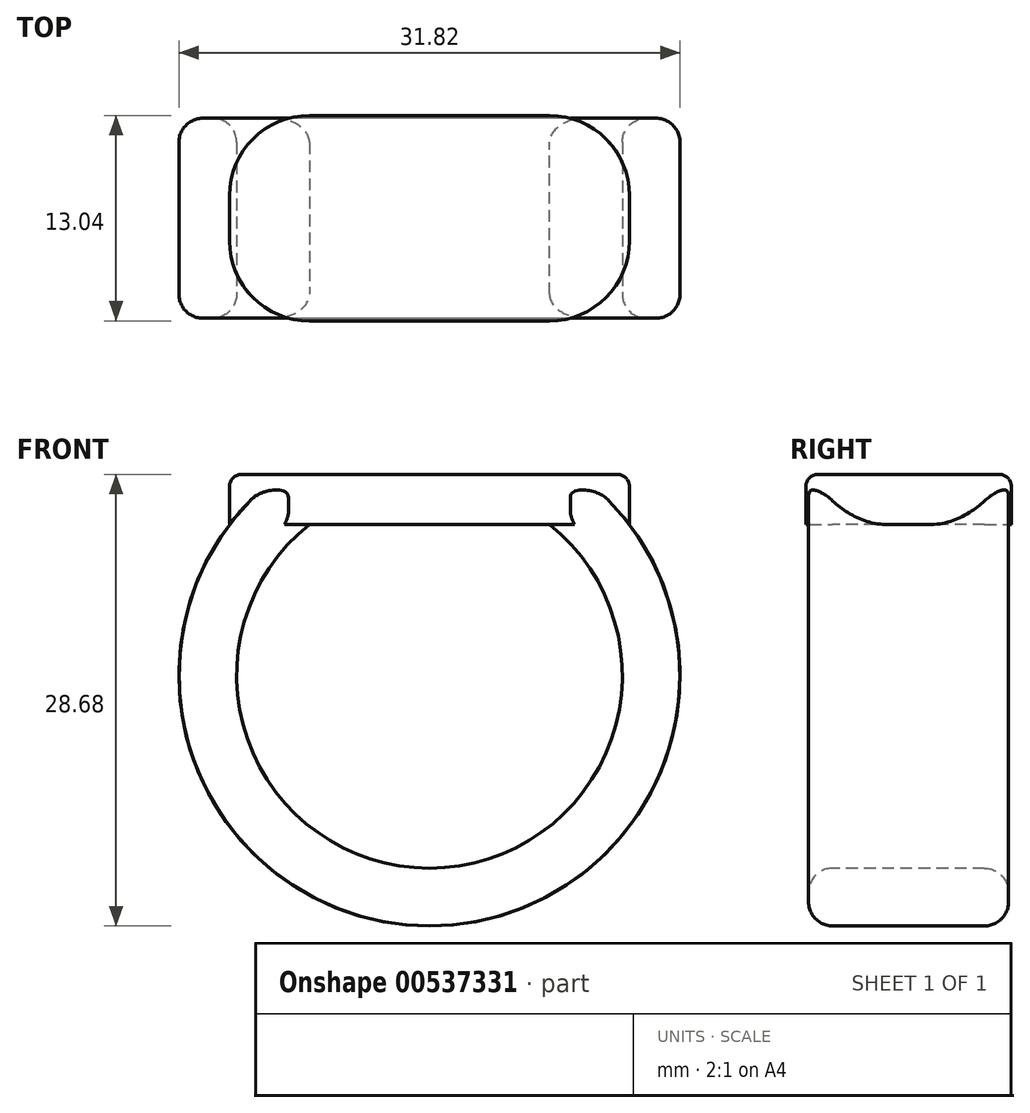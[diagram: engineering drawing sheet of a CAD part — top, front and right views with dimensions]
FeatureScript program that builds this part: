
annotation { "Feature Type Name" : "Feature", "Feature Type Description" : "" }
export const myFeature = defineFeature(function(context is Context, id is Id, definition is map)
    precondition{}
    {
        {
            var Q0;
            Q0=qCreatedBy(makeId("Top.planeOp"),FACE);
            var sketch = newSketch(context, id + "F0", { "sketchPlane" : qUnion([Q0])});
            skLineSegment(sketch, "E0.bottom", {"start": v(12.7, 6.52) * mm, "end": v(-12.7, 6.52) * mm});
            skLineSegment(sketch, "E0.top", {"start": v(12.7, -6.52) * mm, "end": v(-12.7, -6.52) * mm});
            skLineSegment(sketch, "E0.left", {"start": v(12.7, 6.52) * mm, "end": v(12.7, -6.52) * mm});
            skLineSegment(sketch, "E0.right", {"start": v(-12.7, 6.52) * mm, "end": v(-12.7, -6.52) * mm});
            skPoint(sketch, "E0.middle", {"position": v(0, 0) * mm});
            skSolve(sketch);
        }
        {
            var Q0;
            Q0 = qSketchRegion(id + "F0", true);
            extrude(context, id + "F1", {"entities" : qUnion([Q0]), "depth" : 3.17 * mm, "offsetDistance" : 25.4 * mm});
        }
        {
            var Q0;
            Q0=qCreatedBy(makeId("Front.planeOp"),FACE);
            var sketch = newSketch(context, id + "F2", { "sketchPlane" : qUnion([Q0])});
            skArc(sketch, "E1", {"start": v(-10.16, 0) * mm, "mid": v(0, -23.56) * mm, "end": v(10.16, 0) * mm});
            skSolve(sketch);
        }
        {
            var Q0;
            Q0=makeQuery(id+"F1.opExtrude","CAP_FACE",FACE,{"disambiguationData":[OSD([sQuery(id+"F0.wireOp",EDGE,"E0.bottom"),sQuery(id+"F0.wireOp",EDGE,"E0.top"),sQuery(id+"F0.wireOp",EDGE,"E0.left"),sQuery(id+"F0.wireOp",EDGE,"E0.right")])],"isStart":true});
            var sketch = newSketch(context, id + "F3", { "sketchPlane" : qUnion([Q0])});
            skLineSegment(sketch, "E2.bottom", {"start": v(-12.7, -6.35) * mm, "end": v(-7.62, -6.35) * mm});
            skLineSegment(sketch, "E2.top", {"start": v(-12.7, 6.35) * mm, "end": v(-7.62, 6.35) * mm});
            skLineSegment(sketch, "E2.left", {"start": v(-12.7, -6.35) * mm, "end": v(-12.7, 6.35) * mm});
            skLineSegment(sketch, "E2.right", {"start": v(-7.62, -6.35) * mm, "end": v(-7.62, 6.35) * mm});
            skPoint(sketch, "E2.middle", {"position": v(-10.16, 0) * mm});
            skSolve(sketch);
        }
        {
            var Q0;
            Q0 = qSketchRegion(id + "F3", true);
            var Q1;
            Q1 = qConstructionFilter(qBodyType(qCreatedBy(id + "F2" ,EDGE), BodyType.WIRE), ConstructionObject.NO);
            sweep(context, id + "F4", {"operationType" : NewBodyOperationType.ADD, "profiles" : qUnion([Q0]), "path" : qUnion([Q1])});
        }
        {
            var Q0;
            Q0=qCreatedBy(makeId("Front.planeOp"),FACE);
            var sketch = newSketch(context, id + "F5", { "sketchPlane" : qUnion([Q0])});
            skLineSegment(sketch, "E3.0", {"start": v(10.16, 0) * mm, "end": v(7.62, 0) * mm});
            skArc(sketch, "E3.1", {"start": v(10.01, -2.54) * mm, "mid": v(8.9, -1.18) * mm, "end": v(7.62, 0) * mm});
            skLineSegment(sketch, "E3.2", {"start": v(10.01, -2.54) * mm, "end": v(10.16, 0) * mm});
            skPoint(sketch, "E4.orphan", {"position": v(-7.62, 0) * mm});
            skPoint(sketch, "E5.orphan", {"position": v(12.7, 0) * mm});
            skPoint(sketch, "E6.trimOffspring.end.orphan", {"position": v(-12.7, 0) * mm});
            skSolve(sketch);
        }
        {
            var Q0;
            Q0 = qSketchRegion(id + "F5", true);
            var Q1;
            Q1=makeQuery(id+"F4.opSweep","SWEPT_FACE",FACE,{"disambiguationData":[OSD([sQuery(id+"F2.wireOp",EDGE,"E1"),sQuery(id+"F3.wireOp",EDGE,"E2.top")])]});
            var Q2;
            Q2=makeQuery(id+"F4.opSweep","SWEPT_FACE",FACE,{"disambiguationData":[OSD([sQuery(id+"F2.wireOp",EDGE,"E1"),sQuery(id+"F3.wireOp",EDGE,"E2.bottom")])]});
            extrude(context, id + "F6", {"entities" : qUnion([Q0]), "operationType" : NewBodyOperationType.ADD, "endBound" : BoundingType.UP_TO_SURFACE, "depth" : 25.4 * mm, "endBoundEntityFace" : qUnion([Q1]), "offsetDistance" : 25.4 * mm, "hasSecondDirection" : true, "secondDirectionBound" : SecondDirectionBoundingType.UP_TO_SURFACE, "secondDirectionOppositeDirection" : true, "secondDirectionDepth" : 25.4 * mm, "secondDirectionBoundEntityFace" : qUnion([Q2])});
        }
        {
            var Q0;
            Q0=makeQuery(id+"F1.opExtrude","SWEPT_EDGE",EDGE,{"disambiguationData":[OSD([sQuery(id+"F0.wireOp",EDGE,"E0.top"),sQuery(id+"F0.wireOp",EDGE,"E0.left")])]});
            var Q1;
            Q1=makeQuery(id+"F1.opExtrude","SWEPT_EDGE",EDGE,{"disambiguationData":[OSD([sQuery(id+"F0.wireOp",EDGE,"E0.bottom"),sQuery(id+"F0.wireOp",EDGE,"E0.left")])]});
            var Q2;
            Q2=makeQuery(id+"F1.opExtrude","SWEPT_EDGE",EDGE,{"disambiguationData":[OSD([sQuery(id+"F0.wireOp",EDGE,"E0.bottom"),sQuery(id+"F0.wireOp",EDGE,"E0.right")])]});
            var Q3;
            Q3=makeQuery(id+"F1.opExtrude","SWEPT_EDGE",EDGE,{"disambiguationData":[OSD([sQuery(id+"F0.wireOp",EDGE,"E0.top"),sQuery(id+"F0.wireOp",EDGE,"E0.right")])]});
            fillet(context, id + "F7", {"entities" : qUnion([Q0, Q1, Q2, Q3]), "radius" : 5.08 * mm, "tangentPropagation" : true, "allowEdgeOverflow" : false});
        }
        {
            var Q0;
            {var subQ0=sQuery(id+"F3.wireOp",EDGE,"E2.top");var subQ1=sQuery(id+"F2.wireOp",EDGE,"E1");Q0=makeQuery(id+"F6.boolean.opBoolean","MERGE",EDGE,{"derivedFrom":[makeQuery(id+"F4.opSweep","SWEPT_EDGE",EDGE,{"disambiguationData":[OSD([subQ1,subQ0,sQuery(id+"F3.wireOp",EDGE,"E2.right")])]}),makeQuery(id+"F6.opExtrude","TWEAK_EDGE",EDGE,{"derivedFrom":[makeQuery(id+"F4.opSweep","SWEPT_FACE",FACE,{"disambiguationData":[OSD([subQ1,subQ0])]}),makeQuery(id+"F5.imprint","IMPRINT",EDGE,{"derivedFrom":sQuery(id+"F5.wireOp",EDGE,"E3.1")})]})]});}
            var Q1;
            Q1=makeQuery(id+"F4.opSweep","SWEPT_EDGE",EDGE,{"disambiguationData":[OSD([sQuery(id+"F0.wireOp",EDGE,"E0.right"),sQuery(id+"F2.wireOp",EDGE,"E1"),sQuery(id+"F3.wireOp",EDGE,"E2.top"),sQuery(id+"F3.wireOp",EDGE,"E2.left")])]});
            var Q2;
            Q2=makeQuery(id+"F4.opSweep","SWEPT_EDGE",EDGE,{"disambiguationData":[OSD([sQuery(id+"F0.wireOp",EDGE,"E0.right"),sQuery(id+"F2.wireOp",EDGE,"E1"),sQuery(id+"F3.wireOp",EDGE,"E2.bottom"),sQuery(id+"F3.wireOp",EDGE,"E2.left")])]});
            var Q3;
            {var subQ0=sQuery(id+"F3.wireOp",EDGE,"E2.bottom");var subQ1=sQuery(id+"F2.wireOp",EDGE,"E1");Q3=makeQuery(id+"F6.boolean.opBoolean","MERGE",EDGE,{"derivedFrom":[makeQuery(id+"F4.opSweep","SWEPT_EDGE",EDGE,{"disambiguationData":[OSD([subQ1,subQ0,sQuery(id+"F3.wireOp",EDGE,"E2.right")])]}),makeQuery(id+"F6.opExtrude","TWEAK_EDGE",EDGE,{"derivedFrom":[makeQuery(id+"F4.opSweep","SWEPT_FACE",FACE,{"disambiguationData":[OSD([subQ1,subQ0])]}),makeQuery(id+"F5.imprint","IMPRINT",EDGE,{"derivedFrom":sQuery(id+"F5.wireOp",EDGE,"E3.1")})]})]});}
            fillet(context, id + "F8", {"entities" : qUnion([Q0, Q1, Q2, Q3]), "radius" : 1.52 * mm, "tangentPropagation" : true, "allowEdgeOverflow" : false});
        }
        {
            var Q0;
            Q0=makeQuery(id+"F1.opExtrude","CAP_EDGE",EDGE,{"disambiguationData":[OSD([sQuery(id+"F0.wireOp",EDGE,"E0.top")])],"isStart":false});
            var Q1;
            Q1=makeQuery(id+"F1.opExtrude","CAP_EDGE",EDGE,{"disambiguationData":[OSD([sQuery(id+"F0.wireOp",EDGE,"E0.bottom")])],"isStart":false});
            fillet(context, id + "F9", {"entities" : qUnion([Q0, Q1]), "radius" : 0.76 * mm, "tangentPropagation" : true, "allowEdgeOverflow" : false});
        }
    });
